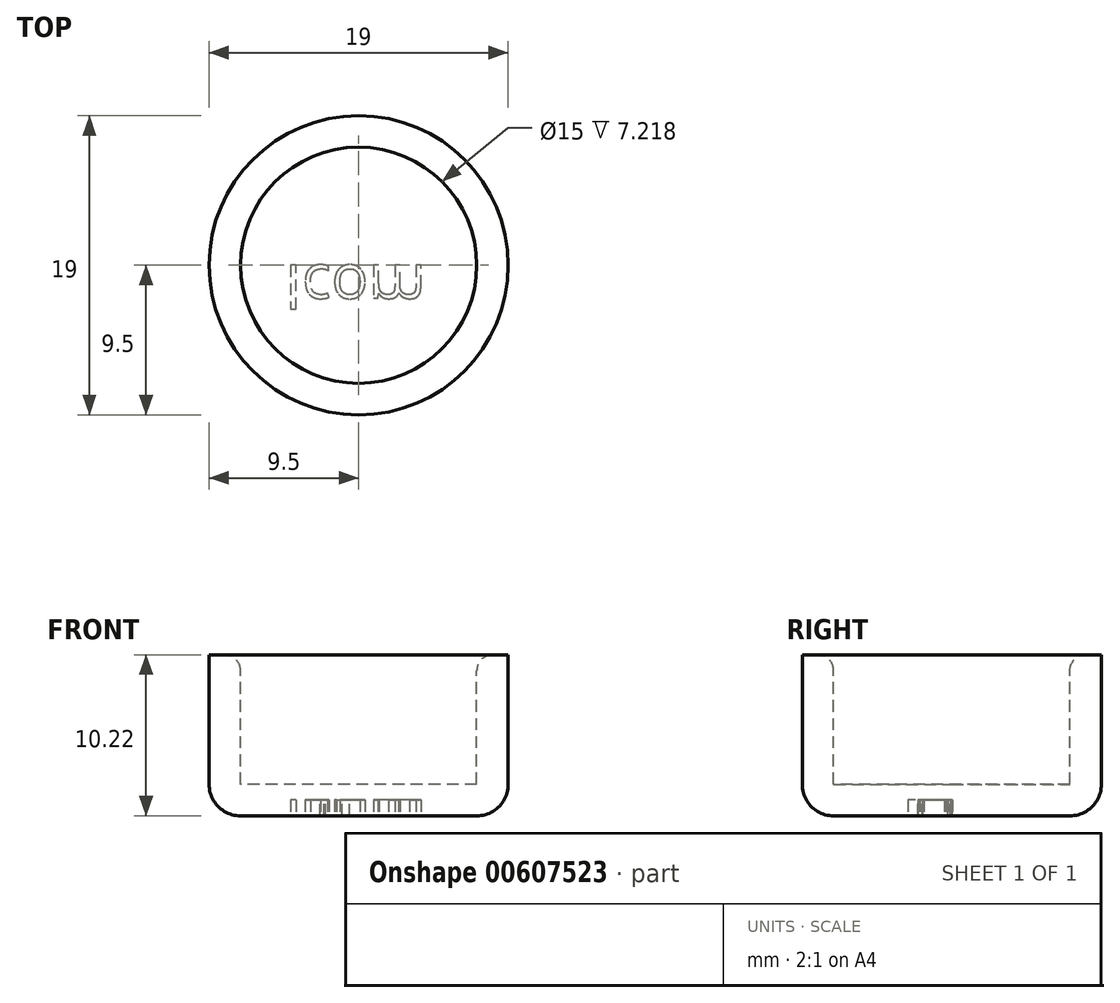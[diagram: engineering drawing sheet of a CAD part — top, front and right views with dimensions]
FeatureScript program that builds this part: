
annotation { "Feature Type Name" : "Feature", "Feature Type Description" : "" }
export const myFeature = defineFeature(function(context is Context, id is Id, definition is map)
    precondition{}
    {
        {
            var Q0;
            Q0=qCreatedBy(makeId("Front.planeOp"),FACE);
            var sketch = newSketch(context, id + "F0", { "sketchPlane" : qUnion([Q0])});
            skLineSegment(sketch, "E0", {"start": v(0, 0) * mm, "end": v(7.5, 0) * mm});
            skLineSegment(sketch, "E1", {"start": v(7.5, 0) * mm, "end": v(7.5, 8.22) * mm});
            skLineSegment(sketch, "E2", {"start": v(7.5, 8.22) * mm, "end": v(9.5, 8.22) * mm});
            skLineSegment(sketch, "E3", {"start": v(9.5, 8.22) * mm, "end": v(9.5, -2) * mm});
            skLineSegment(sketch, "E4", {"start": v(9.5, -2) * mm, "end": v(0, -2) * mm});
            skLineSegment(sketch, "E5", {"start": v(0, -2) * mm, "end": v(0, 0) * mm});
            skLineSegment(sketch, "E6", {"start": v(0, 18.78) * mm, "end": v(0, -22.11) * mm, "construction": true});
            skSolve(sketch);
        }
        {
            var Q0;
            Q0 = qSketchRegion(id + "F0", true);
            var Q1;
            Q1=sQuery(id+"F0.wireOp",EDGE,"E6");
            revolve(context, id + "F1", {"entities" : qUnion([Q0]), "axis" : qUnion([Q1]), "revolveType" : RevolveType.FULL});
        }
        {
            var Q0;
            Q0=makeQuery(id+"F1.opRevolve","SWEPT_EDGE",EDGE,{"disambiguationData":[OSD([sQuery(id+"F0.wireOp",EDGE,"E3"),sQuery(id+"F0.wireOp",EDGE,"E4")])]});
            fillet(context, id + "F2", {"entities" : qUnion([Q0]), "radius" : 2 * mm, "tangentPropagation" : true, "allowEdgeOverflow" : false});
        }
        {
            var Q0;
            Q0=makeQuery(id+"F1.opRevolve","SWEPT_EDGE",EDGE,{"disambiguationData":[OSD([sQuery(id+"F0.wireOp",EDGE,"E1"),sQuery(id+"F0.wireOp",EDGE,"E2")])]});
            fillet(context, id + "F3", {"entities" : qUnion([Q0]), "radius" : 1 * mm, "tangentPropagation" : true, "allowEdgeOverflow" : false});
        }
        {
            var Q0;
            Q0=makeQuery(id+"F1.opRevolve","SWEPT_FACE",FACE,{"disambiguationData":[OSD([sQuery(id+"F0.wireOp",EDGE,"E4")])]});
            var sketch = newSketch(context, id + "F4", { "sketchPlane" : qUnion([Q0])});
            skText(sketch, "E7", { "text": "Icom", "fontName": "OpenSans-Regular.ttf"});
            const initialGuessF4  = {"E7": [-0.0047, 0, 1, 0, 0.00282]};
            skSetInitialGuess(sketch, initialGuessF4);
            skSolve(sketch);
        }
        {
            var Q0;
            Q0 = qSketchRegion(id + "F4", true);
            extrude(context, id + "F5", {"entities" : qUnion([Q0]), "operationType" : NewBodyOperationType.REMOVE, "oppositeDirection" : true, "depth" : 1 * mm, "offsetDistance" : 25 * mm});
        }
    });
